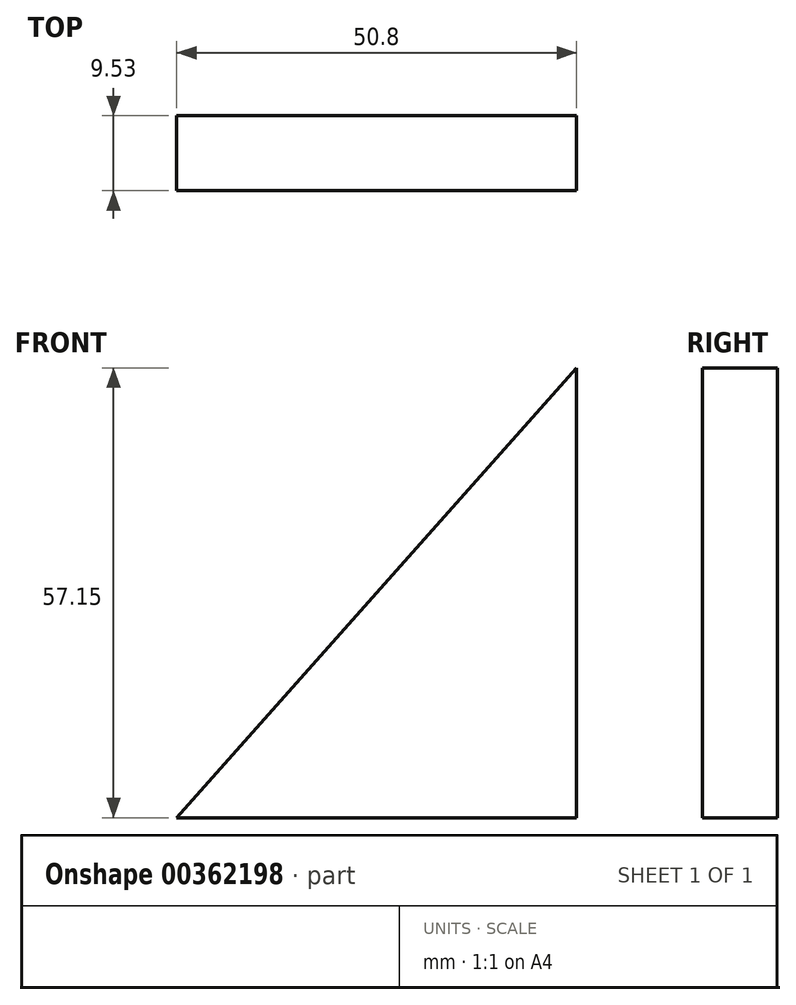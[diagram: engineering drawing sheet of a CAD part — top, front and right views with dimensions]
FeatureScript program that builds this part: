
annotation { "Feature Type Name" : "Feature", "Feature Type Description" : "" }
export const myFeature = defineFeature(function(context is Context, id is Id, definition is map)
    precondition{}
    {
        {
            var Q0;
            Q0=qCreatedBy(makeId("Front.planeOp"),FACE);
            var sketch = newSketch(context, id + "F0", { "sketchPlane" : qUnion([Q0])});
            skLineSegment(sketch, "E0", {"start": v(0, 0) * mm, "end": v(50.8, 0) * mm});
            skLineSegment(sketch, "E1", {"start": v(50.8, 0) * mm, "end": v(50.8, 57.15) * mm});
            skLineSegment(sketch, "E2", {"start": v(0, 0) * mm, "end": v(50.8, 57.15) * mm});
            skSolve(sketch);
        }
        {
            var Q0;
            Q0 = qSketchRegion(id + "F0", true);
            extrude(context, id + "F1", {"entities" : qUnion([Q0]), "depth" : 9.52 * mm});
        }
    });
